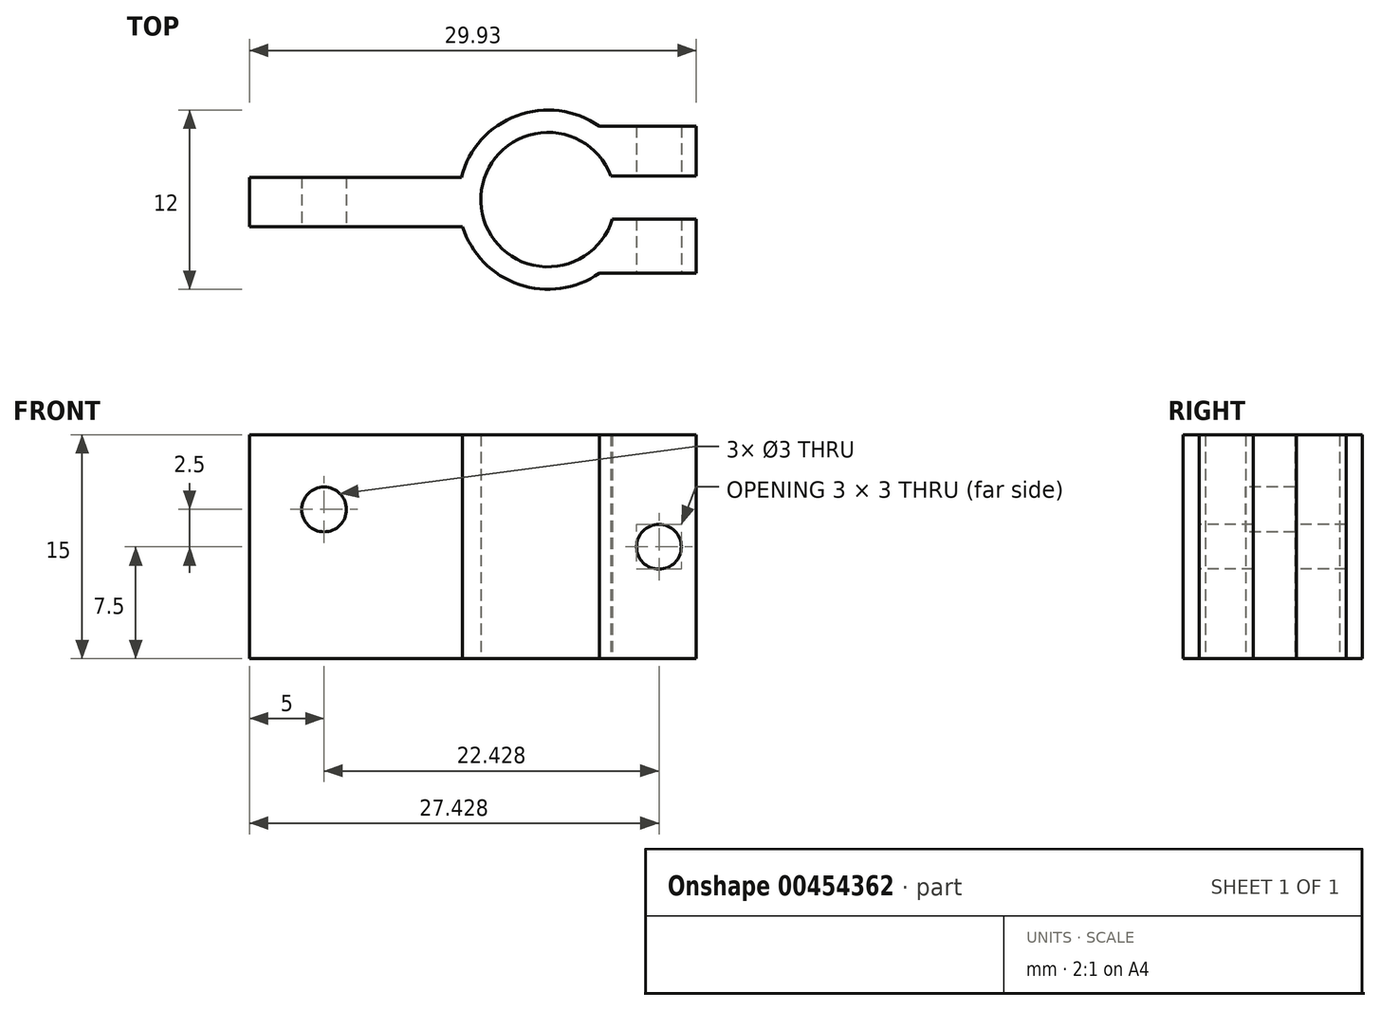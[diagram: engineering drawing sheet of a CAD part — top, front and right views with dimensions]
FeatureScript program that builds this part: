
annotation { "Feature Type Name" : "Feature", "Feature Type Description" : "" }
export const myFeature = defineFeature(function(context is Context, id is Id, definition is map)
    precondition{}
    {
        {
            var Q0;
            Q0=qCreatedBy(makeId("Top.planeOp"),FACE);
            var sketch = newSketch(context, id + "F0", { "sketchPlane" : qUnion([Q0])});
            skLineSegment(sketch, "E0", {"start": v(0, 0) * mm, "end": v(20, 0) * mm, "construction": true});
            skArc(sketch, "E1", {"start": v(24.2, 1.6) * mm, "mid": v(15.5, -0.15) * mm, "end": v(24.3, -1.3) * mm});
            skArc(sketch, "E2", {"start": v(23.43, 4.92) * mm, "mid": v(17.92, 5.63) * mm, "end": v(14.2, 1.5) * mm});
            skLineSegment(sketch, "E3.top", {"start": v(0, 1.5) * mm, "end": v(11.97, 1.5) * mm});
            skLineSegment(sketch, "E3.left", {"start": v(0, 0) * mm, "end": v(0, 1.5) * mm});
            skLineSegment(sketch, "E4.MirrorCS", {"start": v(0, -1.8) * mm, "end": v(11.02, -1.8) * mm});
            skLineSegment(sketch, "E5.MirrorCS", {"start": v(0, 0) * mm, "end": v(0, -1.5) * mm});
            skPoint(sketch, "E6.left.start.orphan", {"position": v(20, -9.06) * mm});
            skLineSegment(sketch, "E7", {"start": v(29.93, 4.92) * mm, "end": v(23.43, 4.92) * mm});
            skLineSegment(sketch, "E8.MirrorCS", {"start": v(29.93, -4.92) * mm, "end": v(23.43, -4.92) * mm});
            skLineSegment(sketch, "E9", {"start": v(11.02, -1.8) * mm, "end": v(14.28, -1.8) * mm});
            skLineSegment(sketch, "E10", {"start": v(11.97, 1.5) * mm, "end": v(14.2, 1.5) * mm});
            skArc(sketch, "E11.trimOffspring", {"start": v(14.28, -1.8) * mm, "mid": v(18.06, -5.68) * mm, "end": v(23.43, -4.92) * mm});
            skLineSegment(sketch, "E12", {"start": v(24.2, 1.6) * mm, "end": v(29.93, 1.6) * mm});
            skLineSegment(sketch, "E13", {"start": v(29.93, 1.6) * mm, "end": v(29.93, 4.92) * mm});
            skLineSegment(sketch, "E14", {"start": v(29.93, -4.92) * mm, "end": v(29.93, -1.3) * mm});
            skLineSegment(sketch, "E15", {"start": v(24.3, -1.3) * mm, "end": v(29.93, -1.3) * mm});
            skLineSegment(sketch, "E16", {"start": v(0, -1.5) * mm, "end": v(0, -1.8) * mm});
            skSolve(sketch);
        }
        {
            var Q0;
            Q0=makeQuery(id+"F0.imprint","IMPRINT",FACE,{"disambiguationData":[TD([[makeQuery(id+"F0.imprint","IMPRINT",EDGE,{"derivedFrom":sQuery(id+"F0.wireOp",EDGE,"E1")}),-1.0]])]});
            extrude(context, id + "F1", {"entities" : qUnion([Q0]), "depth" : 15 * mm});
        }
        {
            var Q0;
            Q0=makeQuery(id+"F1.opExtrude","SWEPT_FACE",FACE,{"disambiguationData":[OSD([sQuery(id+"F0.wireOp",EDGE,"E4.MirrorCS")])]});
            var sketch = newSketch(context, id + "F2", { "sketchPlane" : qUnion([Q0])});
            skLineSegment(sketch, "E17.bottom", {"start": v(0, 15) * mm, "end": v(5, 15) * mm, "construction": true});
            skLineSegment(sketch, "E17.top", {"start": v(0, 10) * mm, "end": v(5, 10) * mm, "construction": true});
            skLineSegment(sketch, "E17.left", {"start": v(0, 15) * mm, "end": v(0, 10) * mm, "construction": true});
            skLineSegment(sketch, "E17.right", {"start": v(5, 15) * mm, "end": v(5, 10) * mm, "construction": true});
            skCircle(sketch, "E18", {"center": v(5, 10) * mm, "radius": 1.5 * mm});
            skSolve(sketch);
        }
        {
            var Q0;
            Q0=makeQuery(id+"F2.imprint","IMPRINT",FACE,{"disambiguationData":[TD([[makeQuery(id+"F2.imprint","IMPRINT",EDGE,{"derivedFrom":sQuery(id+"F2.wireOp",EDGE,"E18")}),1.0]])]});
            extrude(context, id + "F3", {"entities" : qUnion([Q0]), "operationType" : NewBodyOperationType.REMOVE, "oppositeDirection" : true, "depth" : 25 * mm});
        }
        {
            var Q0;
            Q0=makeQuery(id+"F1.opExtrude","SWEPT_FACE",FACE,{"disambiguationData":[OSD([sQuery(id+"F0.wireOp",EDGE,"E8.MirrorCS")])]});
            var sketch = newSketch(context, id + "F4", { "sketchPlane" : qUnion([Q0])});
            skLineSegment(sketch, "E19.bottom", {"start": v(29.93, 15) * mm, "end": v(27.43, 15) * mm, "construction": true});
            skLineSegment(sketch, "E19.top", {"start": v(29.93, 7.5) * mm, "end": v(27.43, 7.5) * mm, "construction": true});
            skLineSegment(sketch, "E19.left", {"start": v(29.93, 15) * mm, "end": v(29.93, 7.5) * mm, "construction": true});
            skLineSegment(sketch, "E19.right", {"start": v(27.43, 15) * mm, "end": v(27.43, 7.5) * mm, "construction": true});
            skCircle(sketch, "E20", {"center": v(27.43, 7.5) * mm, "radius": 1.5 * mm});
            skSolve(sketch);
        }
        {
            var Q0;
            Q0=makeQuery(id+"F4.imprint","IMPRINT",FACE,{"disambiguationData":[TD([[makeQuery(id+"F4.imprint","IMPRINT",EDGE,{"derivedFrom":sQuery(id+"F4.wireOp",EDGE,"E20")}),1.0]])]});
            extrude(context, id + "F5", {"entities" : qUnion([Q0]), "operationType" : NewBodyOperationType.REMOVE, "oppositeDirection" : true, "depth" : 25 * mm});
        }
    });
